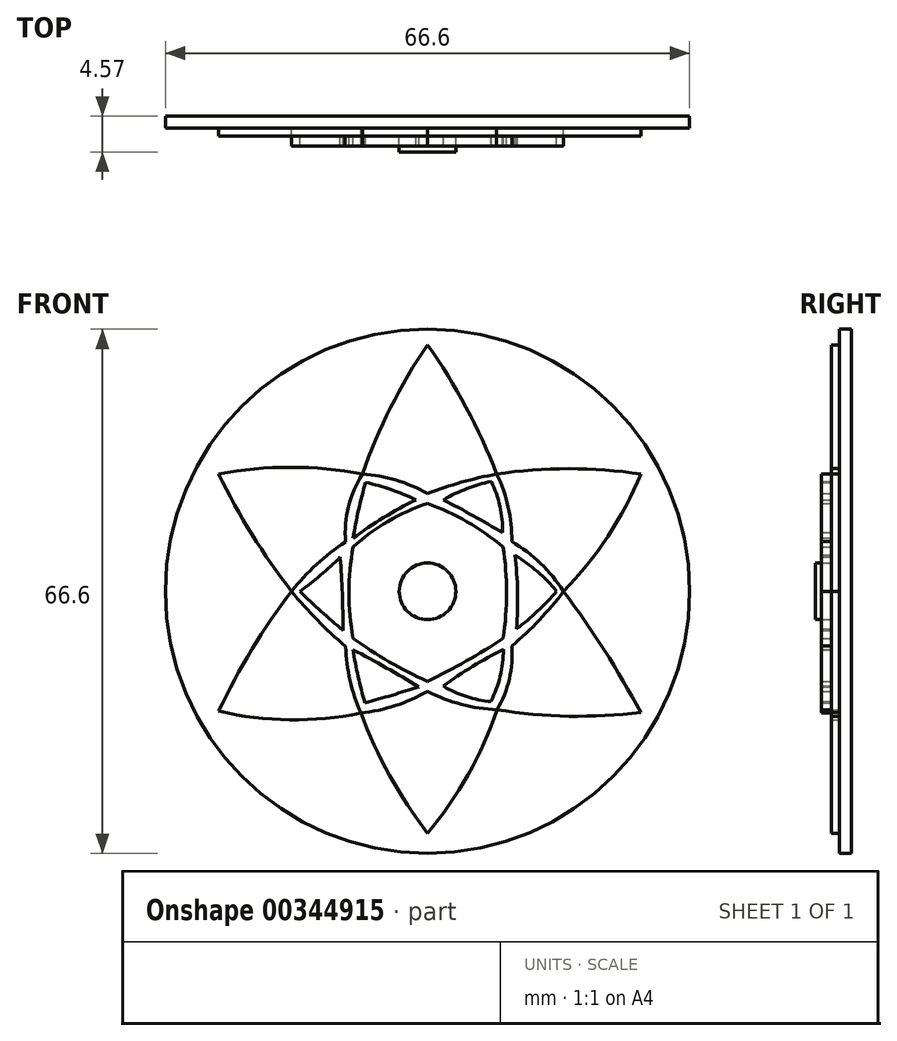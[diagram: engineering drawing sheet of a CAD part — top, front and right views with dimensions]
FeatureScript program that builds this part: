
annotation { "Feature Type Name" : "Feature", "Feature Type Description" : "" }
export const myFeature = defineFeature(function(context is Context, id is Id, definition is map)
    precondition{}
    {
        {
            var Q0;
            Q0=qCreatedBy(makeId("Front.planeOp"),FACE);
            var sketch = newSketch(context, id + "F0", { "sketchPlane" : qUnion([Q0])});
            skSolve(sketch);
        }
        {
            var Q0;
            Q0=qCreatedBy(makeId("Front.planeOp"),FACE);
            var sketch = newSketch(context, id + "F1", { "sketchPlane" : qUnion([Q0])});
            skCircle(sketch, "E0", {"center": v(0, 0) * mm, "radius": 33.3 * mm});
            skSolve(sketch);
        }
        {
            var Q0;
            Q0=makeQuery(id+"F1.imprint","IMPRINT",FACE,{"disambiguationData":[TD([[makeQuery(id+"F1.imprint","IMPRINT",EDGE,{"derivedFrom":sQuery(id+"F1.wireOp",EDGE,"E0")}),1.0]])]});
            var sketch = newSketch(context, id + "F2", { "sketchPlane" : qUnion([Q0])});
            skCircle(sketch, "E1", {"center": v(0, 0) * mm, "radius": 3.6 * mm});
            skSolve(sketch);
        }
        {
            var Q0;
            Q0 = qSketchRegion(id + "F2", true);
            extrude(context, id + "F3", {"entities" : qUnion([Q0]), "depth" : 4.57 * mm});
        }
        {
            var Q0;
            Q0 = qSketchRegion(id + "F0", true);
            var Q1;
            Q1 = qSketchRegion(id + "F1", true);
            extrude(context, id + "F4", {"entities" : qUnion([Q0, Q1]), "operationType" : NewBodyOperationType.ADD, "depth" : 1.52 * mm});
        }
        {
            var Q0;
            Q0=makeQuery(id+"F4.opExtrude","CAP_FACE",FACE,{"disambiguationData":[OSD([sQuery(id+"F1.wireOp",EDGE,"E0")])],"isStart":false});
            var sketch = newSketch(context, id + "F5", { "sketchPlane" : qUnion([Q0])});
            skArc(sketch, "E2", {"start": v(8.79, 14.89) * mm, "mid": v(4.9, 23.37) * mm, "end": v(0, 31.31) * mm});
            skArc(sketch, "E3", {"start": v(0, 31.31) * mm, "mid": v(-4.68, 23.37) * mm, "end": v(-8.29, 14.89) * mm});
            skArc(sketch, "E4", {"start": v(27.09, 14.89) * mm, "mid": v(17.94, 15.57) * mm, "end": v(8.79, 14.89) * mm});
            skArc(sketch, "E5", {"start": v(17.28, 0) * mm, "mid": v(22.9, 6.97) * mm, "end": v(27.09, 14.89) * mm});
            skArc(sketch, "E6", {"start": v(27.09, -15.37) * mm, "mid": v(22.47, -7.5) * mm, "end": v(17.28, 0) * mm});
            skArc(sketch, "E7", {"start": v(8.85, -15.05) * mm, "mid": v(17.96, -15.87) * mm, "end": v(27.09, -15.37) * mm});
            skArc(sketch, "E8", {"start": v(0, -30.73) * mm, "mid": v(5.16, -23.3) * mm, "end": v(8.85, -15.05) * mm});
            skArc(sketch, "E9", {"start": v(-8.29, 14.89) * mm, "mid": v(-17.4, 15.76) * mm, "end": v(-26.52, 14.89) * mm});
            skArc(sketch, "E10", {"start": v(-26.52, 14.89) * mm, "mid": v(-22.29, 7.2) * mm, "end": v(-17.27, 0) * mm});
            skArc(sketch, "E11", {"start": v(-17.27, 0) * mm, "mid": v(-22.32, -7.36) * mm, "end": v(-26.52, -15.23) * mm});
            skArc(sketch, "E12", {"start": v(9.54, 7.45) * mm, "mid": v(9.2, 10.79) * mm, "end": v(8.1, 13.97) * mm});
            skArc(sketch, "E13", {"start": v(17.28, 0) * mm, "mid": v(14.36, 3.54) * mm, "end": v(10.71, 6.32) * mm});
            skArc(sketch, "E14", {"start": v(16.4, 0) * mm, "mid": v(13.94, 2.51) * mm, "end": v(11.1, 4.6) * mm});
            skArc(sketch, "E15", {"start": v(11.32, -4.76) * mm, "mid": v(14, -2.52) * mm, "end": v(16.4, 0) * mm});
            skArc(sketch, "E16", {"start": v(11.32, -4.76) * mm, "mid": v(11.44, -0.07) * mm, "end": v(11.1, 4.6) * mm});
            skArc(sketch, "E17", {"start": v(8.85, -15.05) * mm, "mid": v(10.4, -11.13) * mm, "end": v(10.7, -6.92) * mm});
            skArc(sketch, "E18", {"start": v(8.05, -14.02) * mm, "mid": v(9.22, -10.8) * mm, "end": v(9.63, -7.39) * mm});
            skArc(sketch, "E19", {"start": v(2.02, -12.05) * mm, "mid": v(4.93, -13.36) * mm, "end": v(8.05, -14.02) * mm});
            skArc(sketch, "E20", {"start": v(9.63, -7.39) * mm, "mid": v(5.72, -9.55) * mm, "end": v(2.02, -12.05) * mm});
            skArc(sketch, "E21", {"start": v(10.71, 6.32) * mm, "mid": v(10.25, 10.72) * mm, "end": v(8.79, 14.89) * mm});
            skArc(sketch, "E22", {"start": v(9.54, 7.45) * mm, "mid": v(5.83, 9.59) * mm, "end": v(2.06, 11.62) * mm});
            skArc(sketch, "E23", {"start": v(8.1, 13.97) * mm, "mid": v(4.98, 13.05) * mm, "end": v(2.06, 11.62) * mm});
            skArc(sketch, "E24", {"start": v(-7.93, -14.16) * mm, "mid": v(-4.5, -13.2) * mm, "end": v(-1.11, -12.13) * mm});
            skArc(sketch, "E25", {"start": v(-1.11, -12.13) * mm, "mid": v(-5.25, -9.72) * mm, "end": v(-9.46, -7.42) * mm});
            skArc(sketch, "E26", {"start": v(-9.46, -7.42) * mm, "mid": v(-8.82, -10.82) * mm, "end": v(-7.93, -14.16) * mm});
            skArc(sketch, "E27", {"start": v(-16.23, 0) * mm, "mid": v(-13.53, -2.53) * mm, "end": v(-10.75, -4.95) * mm});
            skArc(sketch, "E28", {"start": v(-16.23, 0) * mm, "mid": v(-13.56, 2.05) * mm, "end": v(-11.1, 4.33) * mm});
            skArc(sketch, "E29", {"start": v(-10.75, -4.95) * mm, "mid": v(-10.82, -0.3) * mm, "end": v(-11.1, 4.33) * mm});
            skArc(sketch, "E30", {"start": v(-7.86, 13.84) * mm, "mid": v(-8.77, 10.32) * mm, "end": v(-9.46, 6.75) * mm});
            skArc(sketch, "E31", {"start": v(-1.48, 11.62) * mm, "mid": v(-4.6, 12.9) * mm, "end": v(-7.86, 13.84) * mm});
            skArc(sketch, "E32", {"start": v(-1.48, 11.62) * mm, "mid": v(-5.57, 9.35) * mm, "end": v(-9.46, 6.75) * mm});
            skArc(sketch, "E33", {"start": v(8.79, 14.89) * mm, "mid": v(4.33, 13.86) * mm, "end": v(0, 12.4) * mm});
            skArc(sketch, "E34", {"start": v(0, 12.4) * mm, "mid": v(-4, 14.13) * mm, "end": v(-8.29, 14.89) * mm});
            skArc(sketch, "E35", {"start": v(-8.29, 14.89) * mm, "mid": v(-10.05, 10.75) * mm, "end": v(-10.41, 6.27) * mm});
            skArc(sketch, "E36", {"start": v(-10.41, 6.27) * mm, "mid": v(-14.1, 3.41) * mm, "end": v(-17.27, 0) * mm});
            skArc(sketch, "E37", {"start": v(10.7, -6.92) * mm, "mid": v(14.2, -3.66) * mm, "end": v(17.28, 0) * mm});
            skArc(sketch, "E38", {"start": v(0, -12.73) * mm, "mid": v(4.3, -14.35) * mm, "end": v(8.85, -15.05) * mm});
            skArc(sketch, "E39", {"start": v(-17.27, 0) * mm, "mid": v(-14, -3.67) * mm, "end": v(-10.4, -7.01) * mm});
            skArc(sketch, "E40", {"start": v(-8.47, -15.47) * mm, "mid": v(-4.8, -23.41) * mm, "end": v(0, -30.73) * mm});
            skArc(sketch, "E41", {"start": v(-26.52, -15.23) * mm, "mid": v(-17.5, -16.34) * mm, "end": v(-8.47, -15.47) * mm});
            skArc(sketch, "E42", {"start": v(-8.47, -15.47) * mm, "mid": v(-4.1, -14.53) * mm, "end": v(0, -12.73) * mm});
            skArc(sketch, "E43", {"start": v(-10.4, -7.01) * mm, "mid": v(-9.83, -11.33) * mm, "end": v(-8.47, -15.47) * mm});
            skArc(sketch, "E44", {"start": v(0, -11.42) * mm, "mid": v(4.9, -8.88) * mm, "end": v(9.61, -5.97) * mm});
            skArc(sketch, "E45", {"start": v(9.61, -5.97) * mm, "mid": v(10.04, -0.17) * mm, "end": v(9.61, 5.64) * mm});
            skArc(sketch, "E46", {"start": v(9.61, 5.64) * mm, "mid": v(5.04, 8.82) * mm, "end": v(0, 11.17) * mm});
            skArc(sketch, "E47", {"start": v(0, 11.17) * mm, "mid": v(-5.01, 8.9) * mm, "end": v(-9.46, 5.64) * mm});
            skArc(sketch, "E48", {"start": v(-9.46, -5.97) * mm, "mid": v(-4.88, -8.96) * mm, "end": v(0, -11.42) * mm});
            skArc(sketch, "E49", {"start": v(-9.46, 5.64) * mm, "mid": v(-9.98, -0.17) * mm, "end": v(-9.46, -5.97) * mm});
            skSolve(sketch);
        }
        {
            var Q0;
            Q0=makeQuery(id+"F5.imprint","IMPRINT",FACE,{"disambiguationData":[TD([[makeQuery(id+"F5.imprint","IMPRINT",EDGE,{"derivedFrom":sQuery(id+"F5.wireOp",EDGE,"E12")}),-1.0]])]});
            extrude(context, id + "F6", {"entities" : qUnion([Q0]), "operationType" : NewBodyOperationType.ADD, "depth" : 2.3 * mm});
        }
        {
            var Q0;
            Q0=makeQuery(id+"F5.imprint","IMPRINT",FACE,{"disambiguationData":[TD([[makeQuery(id+"F5.imprint","IMPRINT",EDGE,{"derivedFrom":sQuery(id+"F5.wireOp",EDGE,"E9")}),1.0]])]});
            var Q1;
            Q1=makeQuery(id+"F5.imprint","IMPRINT",FACE,{"disambiguationData":[TD([[makeQuery(id+"F5.imprint","IMPRINT",EDGE,{"derivedFrom":sQuery(id+"F5.wireOp",EDGE,"E2")}),1.0]])]});
            var Q2;
            Q2=makeQuery(id+"F5.imprint","IMPRINT",FACE,{"disambiguationData":[TD([[makeQuery(id+"F5.imprint","IMPRINT",EDGE,{"derivedFrom":sQuery(id+"F5.wireOp",EDGE,"E4")}),1.0]])]});
            var Q3;
            Q3=makeQuery(id+"F5.imprint","IMPRINT",FACE,{"disambiguationData":[TD([[makeQuery(id+"F5.imprint","IMPRINT",EDGE,{"derivedFrom":sQuery(id+"F5.wireOp",EDGE,"E6")}),1.0]])]});
            var Q4;
            Q4=makeQuery(id+"F5.imprint","IMPRINT",FACE,{"disambiguationData":[TD([[makeQuery(id+"F5.imprint","IMPRINT",EDGE,{"derivedFrom":sQuery(id+"F5.wireOp",EDGE,"E8")}),1.0]])]});
            var Q5;
            Q5=makeQuery(id+"F5.imprint","IMPRINT",FACE,{"disambiguationData":[TD([[makeQuery(id+"F5.imprint","IMPRINT",EDGE,{"derivedFrom":sQuery(id+"F5.wireOp",EDGE,"E11")}),1.0]])]});
            var Q6;
            Q6=makeQuery(id+"F5.imprint","IMPRINT",FACE,{"disambiguationData":[TD([[makeQuery(id+"F5.imprint","IMPRINT",EDGE,{"derivedFrom":sQuery(id+"F5.wireOp",EDGE,"E24")}),1.0]])]});
            var Q7;
            Q7=makeQuery(id+"F5.imprint","IMPRINT",FACE,{"disambiguationData":[TD([[makeQuery(id+"F5.imprint","IMPRINT",EDGE,{"derivedFrom":sQuery(id+"F5.wireOp",EDGE,"E18")}),1.0]])]});
            var Q8;
            Q8=makeQuery(id+"F5.imprint","IMPRINT",FACE,{"disambiguationData":[TD([[makeQuery(id+"F5.imprint","IMPRINT",EDGE,{"derivedFrom":sQuery(id+"F5.wireOp",EDGE,"E44")}),1.0]])]});
            var Q9;
            Q9=makeQuery(id+"F5.imprint","IMPRINT",FACE,{"disambiguationData":[TD([[makeQuery(id+"F5.imprint","IMPRINT",EDGE,{"derivedFrom":sQuery(id+"F5.wireOp",EDGE,"E14")}),1.0]])]});
            var Q10;
            Q10=makeQuery(id+"F5.imprint","IMPRINT",FACE,{"disambiguationData":[TD([[makeQuery(id+"F5.imprint","IMPRINT",EDGE,{"derivedFrom":sQuery(id+"F5.wireOp",EDGE,"E30")}),1.0]])]});
            var Q11;
            Q11=makeQuery(id+"F5.imprint","IMPRINT",FACE,{"disambiguationData":[TD([[makeQuery(id+"F5.imprint","IMPRINT",EDGE,{"derivedFrom":sQuery(id+"F5.wireOp",EDGE,"E12")}),1.0]])]});
            var Q12;
            Q12=makeQuery(id+"F5.imprint","IMPRINT",FACE,{"disambiguationData":[TD([[makeQuery(id+"F5.imprint","IMPRINT",EDGE,{"derivedFrom":sQuery(id+"F5.wireOp",EDGE,"E27")}),1.0]])]});
            extrude(context, id + "F7", {"entities" : qUnion([Q0, Q1, Q2, Q3, Q4, Q5, Q6, Q7, Q8, Q9, Q10, Q11, Q12]), "operationType" : NewBodyOperationType.ADD, "depth" : 1.02 * mm});
        }
    });
